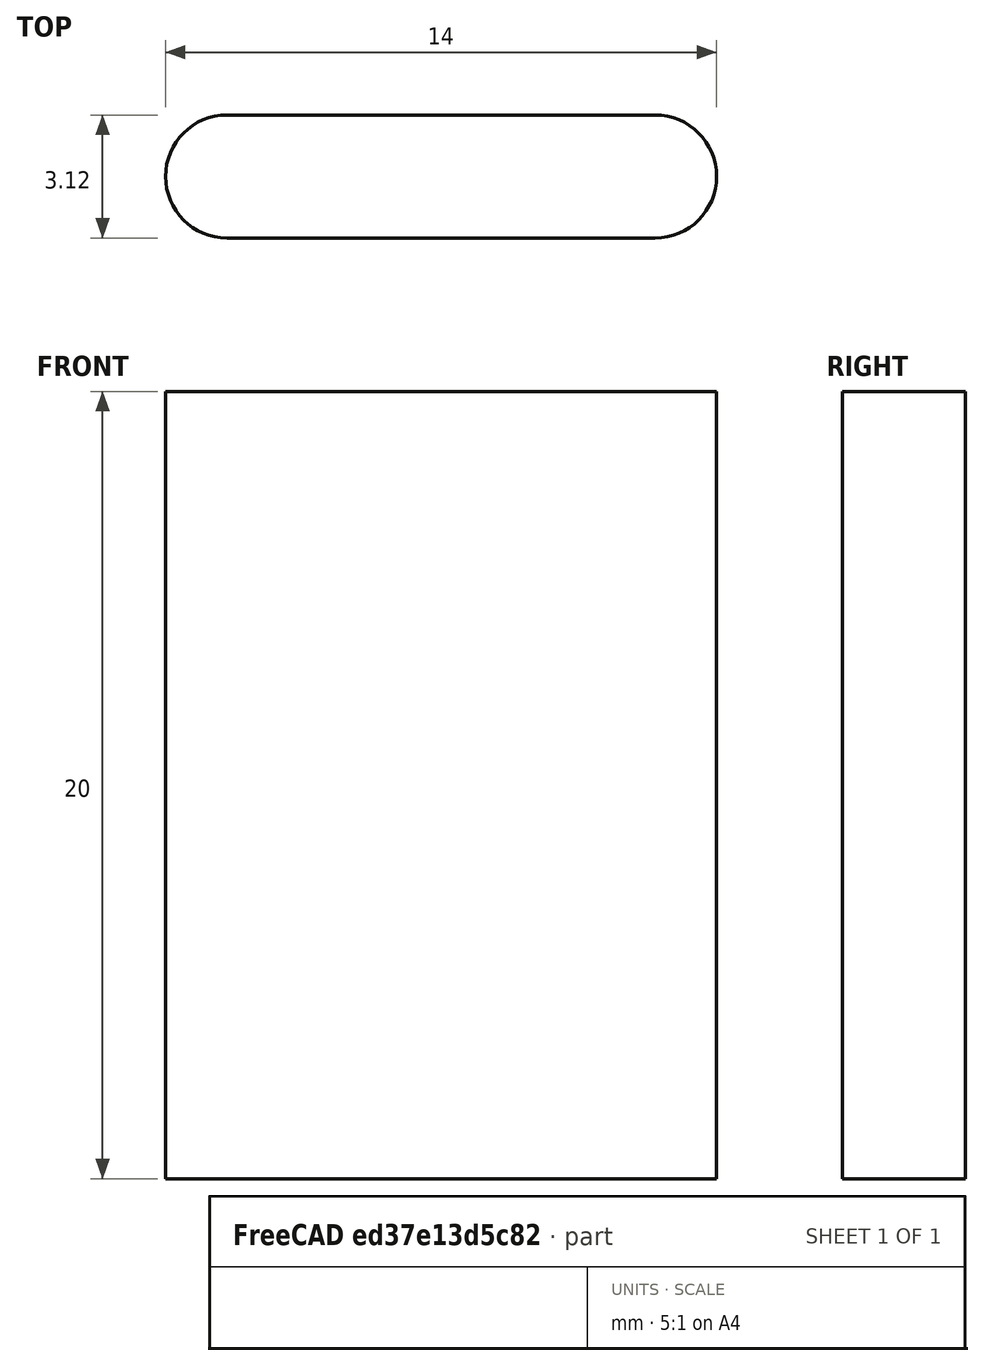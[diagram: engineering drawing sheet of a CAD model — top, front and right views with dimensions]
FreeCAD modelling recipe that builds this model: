
FCSTD DOCUMENT  (FreeCAD 0.19R24276 (Git))
Label: BLDC_axis_fix
License: All rights reserved
LicenseURL: http://en.wikipedia.org/wiki/All_rights_reserved
objects: Sketcher::SketchObject×1, PartDesign::Pad×1, PartDesign::Body×1
note: 4 computed .brp shape members not serialized (recipe doc carries the construction recipe); baked Part::Feature solids carry a one-line shape summary decoded from their .brp

FEATURE [Sketcher::SketchObject] Sketch
  FullyConstrained = true
  MapMode = 5
  Support = -> [XY_Plane]
  sketch-geometry (6):
    g0: LineSegment StartX=1.5625 StartY=0 StartZ=0 EndX=12.4375 EndY=0 EndZ=0
    g1: LineSegment StartX=12.4375 StartY=3.125 StartZ=0 EndX=1.5625 EndY=3.125 EndZ=0
    g2: ArcOfCircle CenterX=1.5625 CenterY=1.5625 CenterZ=0 NormalX=0 NormalY=0 NormalZ=1 AngleXU=0 Radius=1.5625 StartAngle=1.5708 EndAngle=4.71239
    g3: ArcOfCircle CenterX=12.4375 CenterY=1.5625 CenterZ=0 NormalX=0 NormalY=0 NormalZ=1 AngleXU=0 Radius=1.5625 StartAngle=4.71239 EndAngle=7.85398
    g4: LineSegment StartX=1.5625 StartY=1.5625 StartZ=0 EndX=2e-16 EndY=1.5625 EndZ=0
    g5: LineSegment StartX=12.4375 StartY=1.5625 StartZ=0 EndX=14 EndY=1.5625 EndZ=0
  constraints (20):
    c: Horizontal(g0)
    c: Horizontal(g1)
    c: Coincident(g4,g2)
    c: Horizontal(g4)
    c: DistanceX(g-1,g2) = 1.5625
    c: Coincident(g5,g3)
    c: Horizontal(g5)
    c: Coincident(g2,g1)
    c: Coincident(g2,g0)
    c: Coincident(g3,g0)
    c: Coincident(g3,g1)
    c: Horizontal(g2,g-1)
    c: Vertical(g2,g2)
    c: Vertical(g3,g3)
    c: DistanceY(g2,g2) = 3.125
    c: Vertical(g2,g2)
    c: Vertical(g3,g3)
    c: PointOnObject(g4,g2)
    c: PointOnObject(g5,g3)
    c: DistanceX(g4,g5) = 14
FEATURE [PartDesign::Pad] Pad
  Direction = (1,1,1)
  Length = 20
  Length2 = 100
  Profile = -> Sketch
  Type = 0
FEATURE [PartDesign::Body] Body
  Group = -> [Sketch,Pad]
  Origin = -> Origin
  Tip = -> Pad
